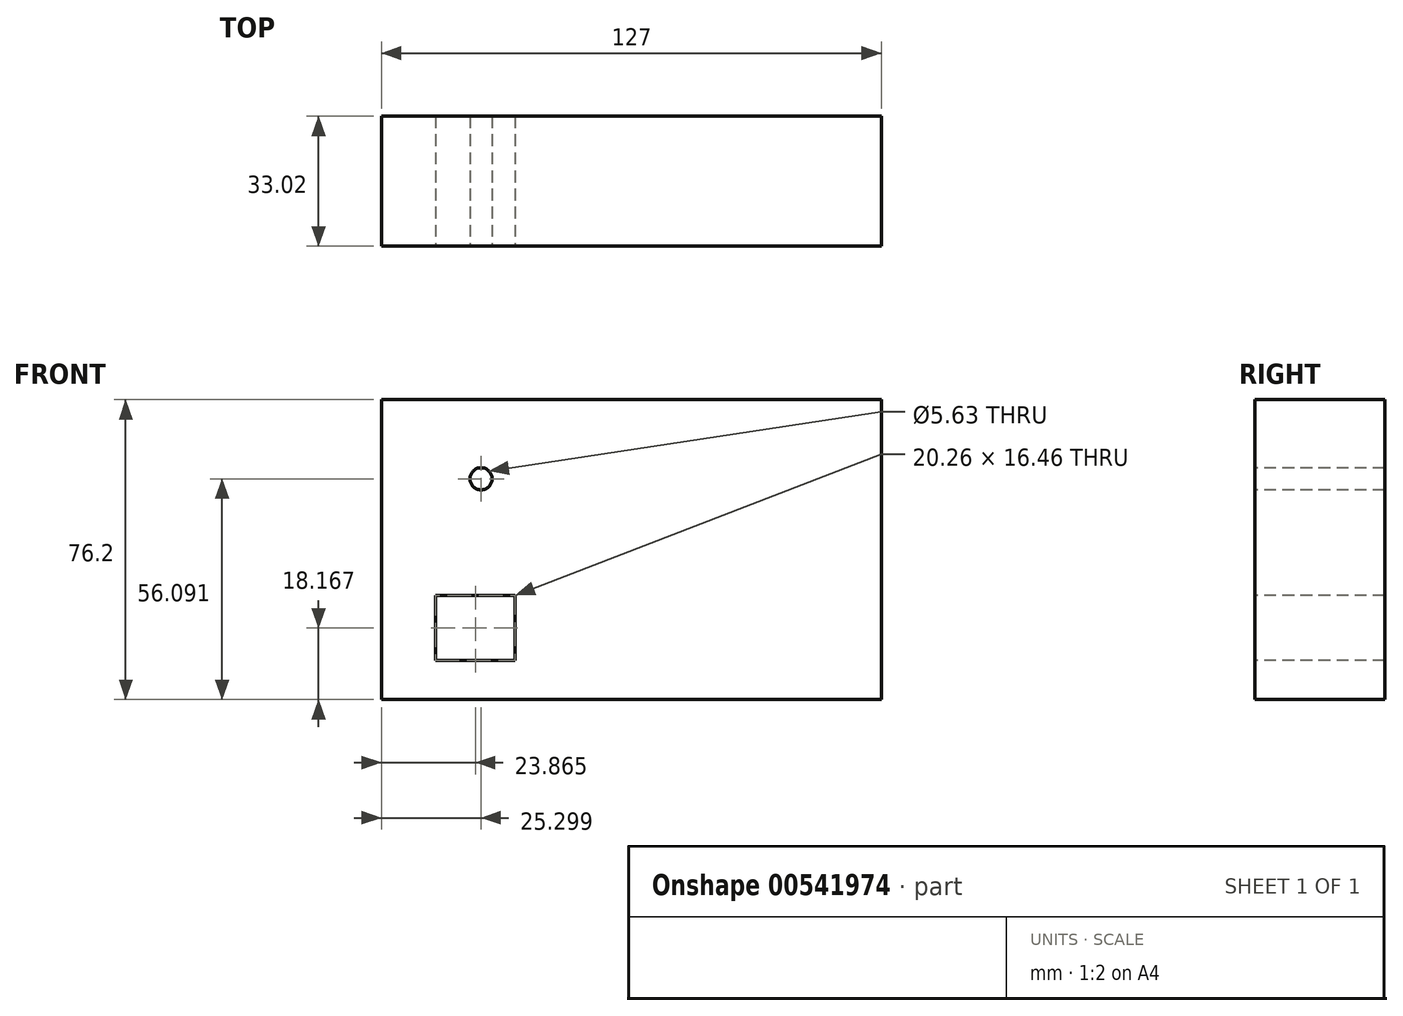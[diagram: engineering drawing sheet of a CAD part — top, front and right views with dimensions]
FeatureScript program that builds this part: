
annotation { "Feature Type Name" : "Feature", "Feature Type Description" : "" }
export const myFeature = defineFeature(function(context is Context, id is Id, definition is map)
    precondition{}
    {
        {
            var Q0;
            Q0=qCreatedBy(makeId("Front.planeOp"),FACE);
            var sketch = newSketch(context, id + "F0", { "sketchPlane" : qUnion([Q0])});
            skLineSegment(sketch, "E0.bottom", {"start": v(-63.5, 38.1) * mm, "end": v(63.5, 38.1) * mm});
            skLineSegment(sketch, "E0.top", {"start": v(-63.5, -38.1) * mm, "end": v(63.5, -38.1) * mm});
            skLineSegment(sketch, "E0.left", {"start": v(-63.5, 38.1) * mm, "end": v(-63.5, -38.1) * mm});
            skLineSegment(sketch, "E0.right", {"start": v(63.5, 38.1) * mm, "end": v(63.5, -38.1) * mm});
            skPoint(sketch, "E0.middle", {"position": v(0, 0) * mm});
            skSolve(sketch);
        }
        {
            var Q0;
            Q0=makeQuery(id+"F0.imprint","IMPRINT",FACE,{"disambiguationData":[TD([[makeQuery(id+"F0.imprint","IMPRINT",EDGE,{"derivedFrom":sQuery(id+"F0.wireOp",EDGE,"E0.bottom")}),-1.0]])]});
            extrude(context, id + "F1", {"entities" : qUnion([Q0]), "endBound" : BoundingType.SYMMETRIC, "depth" : 7.62 * mm, "offsetDistance" : 25.4 * mm});
        }
        {
            var Q0;
            Q0=makeQuery(id+"F1.opExtrude","CAP_FACE",FACE,{"disambiguationData":[OSD([sQuery(id+"F0.wireOp",EDGE,"E0.bottom"),sQuery(id+"F0.wireOp",EDGE,"E0.top"),sQuery(id+"F0.wireOp",EDGE,"E0.left"),sQuery(id+"F0.wireOp",EDGE,"E0.right")])],"isStart":false});
            var sketch = newSketch(context, id + "F2", { "sketchPlane" : qUnion([Q0])});
            skCircle(sketch, "E1", {"center": v(-38.2, 18) * mm, "radius": 2.81 * mm});
            skSolve(sketch);
        }
        {
            var Q0;
            Q0 = qSketchRegion(id + "F2", true);
            extrude(context, id + "F3", {"entities" : qUnion([Q0]), "operationType" : NewBodyOperationType.REMOVE, "oppositeDirection" : true, "depth" : 25.4 * mm, "offsetDistance" : 25.4 * mm});
        }
        {
            var Q0;
            Q0=makeQuery(id+"F1.opExtrude","CAP_FACE",FACE,{"disambiguationData":[OSD([sQuery(id+"F0.wireOp",EDGE,"E0.bottom"),sQuery(id+"F0.wireOp",EDGE,"E0.top"),sQuery(id+"F0.wireOp",EDGE,"E0.left"),sQuery(id+"F0.wireOp",EDGE,"E0.right")])],"isStart":false});
            var sketch = newSketch(context, id + "F4", { "sketchPlane" : qUnion([Q0])});
            skLineSegment(sketch, "E2.bottom", {"start": v(-49.76, -11.7) * mm, "end": v(-29.5, -11.7) * mm});
            skLineSegment(sketch, "E2.top", {"start": v(-49.76, -28.17) * mm, "end": v(-29.5, -28.17) * mm});
            skLineSegment(sketch, "E2.left", {"start": v(-49.76, -11.7) * mm, "end": v(-49.76, -28.17) * mm});
            skLineSegment(sketch, "E2.right", {"start": v(-29.5, -11.7) * mm, "end": v(-29.5, -28.17) * mm});
            skSolve(sketch);
        }
        {
            var Q0;
            Q0 = qSketchRegion(id + "F4", true);
            extrude(context, id + "F5", {"entities" : qUnion([Q0]), "operationType" : NewBodyOperationType.REMOVE, "oppositeDirection" : true, "depth" : 101.6 * mm, "offsetDistance" : 25.4 * mm});
        }
        {
            var Q0;
            Q0=makeQuery(id+"F1.opExtrude","CAP_FACE",FACE,{"disambiguationData":[OSD([sQuery(id+"F0.wireOp",EDGE,"E0.bottom"),sQuery(id+"F0.wireOp",EDGE,"E0.top"),sQuery(id+"F0.wireOp",EDGE,"E0.left"),sQuery(id+"F0.wireOp",EDGE,"E0.right")])],"isStart":false});
            var sketch = newSketch(context, id + "F6", { "sketchPlane" : qUnion([Q0])});
            skArc(sketch, "E3", {"start": v(-3.22, 8.86) * mm, "mid": v(-8.9, 14.37) * mm, "end": v(-14.4, 8.7) * mm});
            skLineSegment(sketch, "E4", {"start": v(-3.22, 8.86) * mm, "end": v(-0.43, 8.86) * mm});
            skLineSegment(sketch, "E5", {"start": v(-14.4, 8.7) * mm, "end": v(-17.19, 8.7) * mm});
            skLineSegment(sketch, "E6.0", {"start": v(-16.01, 10.51) * mm, "end": v(-17.19, 10.51) * mm});
            skArc(sketch, "E6.1", {"start": v(-1.65, 10.68) * mm, "mid": v(-8.9, 16.19) * mm, "end": v(-16.01, 10.51) * mm});
            skLineSegment(sketch, "E6.2", {"start": v(-1.65, 10.68) * mm, "end": v(-0.43, 10.68) * mm});
            skLineSegment(sketch, "E7", {"start": v(-17.19, 8.7) * mm, "end": v(-17.19, 10.51) * mm});
            skLineSegment(sketch, "E8", {"start": v(-0.43, 8.86) * mm, "end": v(-0.43, 10.68) * mm});
            skSolve(sketch);
        }
        {
            var Q0;
            Q0=makeQuery(id+"F6.imprint","IMPRINT",FACE,{"disambiguationData":[TD([[makeQuery(id+"F6.imprint","IMPRINT",EDGE,{"derivedFrom":sQuery(id+"F6.wireOp",EDGE,"E3")}),-1.0]])]});
            var Q1;
            Q1=makeQuery(id+"F6.imprint","IMPRINT",FACE,{"disambiguationData":[TD([[makeQuery(id+"F6.imprint","IMPRINT",EDGE,{"derivedFrom":sQuery(id+"F6.wireOp",EDGE,"E3")}),1.0]])]});
            var Q2;
            Q2=makeQuery(id+"F1.opExtrude","CAP_FACE",FACE,{"disambiguationData":[OSD([sQuery(id+"F0.wireOp",EDGE,"E0.bottom"),sQuery(id+"F0.wireOp",EDGE,"E0.top"),sQuery(id+"F0.wireOp",EDGE,"E0.left"),sQuery(id+"F0.wireOp",EDGE,"E0.right")])],"isStart":false});
            var Q3;
            Q3=makeQuery(id+"F1.opExtrude","CAP_FACE",FACE,{"disambiguationData":[OSD([sQuery(id+"F0.wireOp",EDGE,"E0.bottom"),sQuery(id+"F0.wireOp",EDGE,"E0.top"),sQuery(id+"F0.wireOp",EDGE,"E0.left"),sQuery(id+"F0.wireOp",EDGE,"E0.right")])],"isStart":true});
            extrude(context, id + "F7", {"entities" : qUnion([Q0, Q1, Q2, Q3]), "operationType" : NewBodyOperationType.ADD, "depth" : 25.4 * mm, "offsetDistance" : 25.4 * mm});
        }
    });
